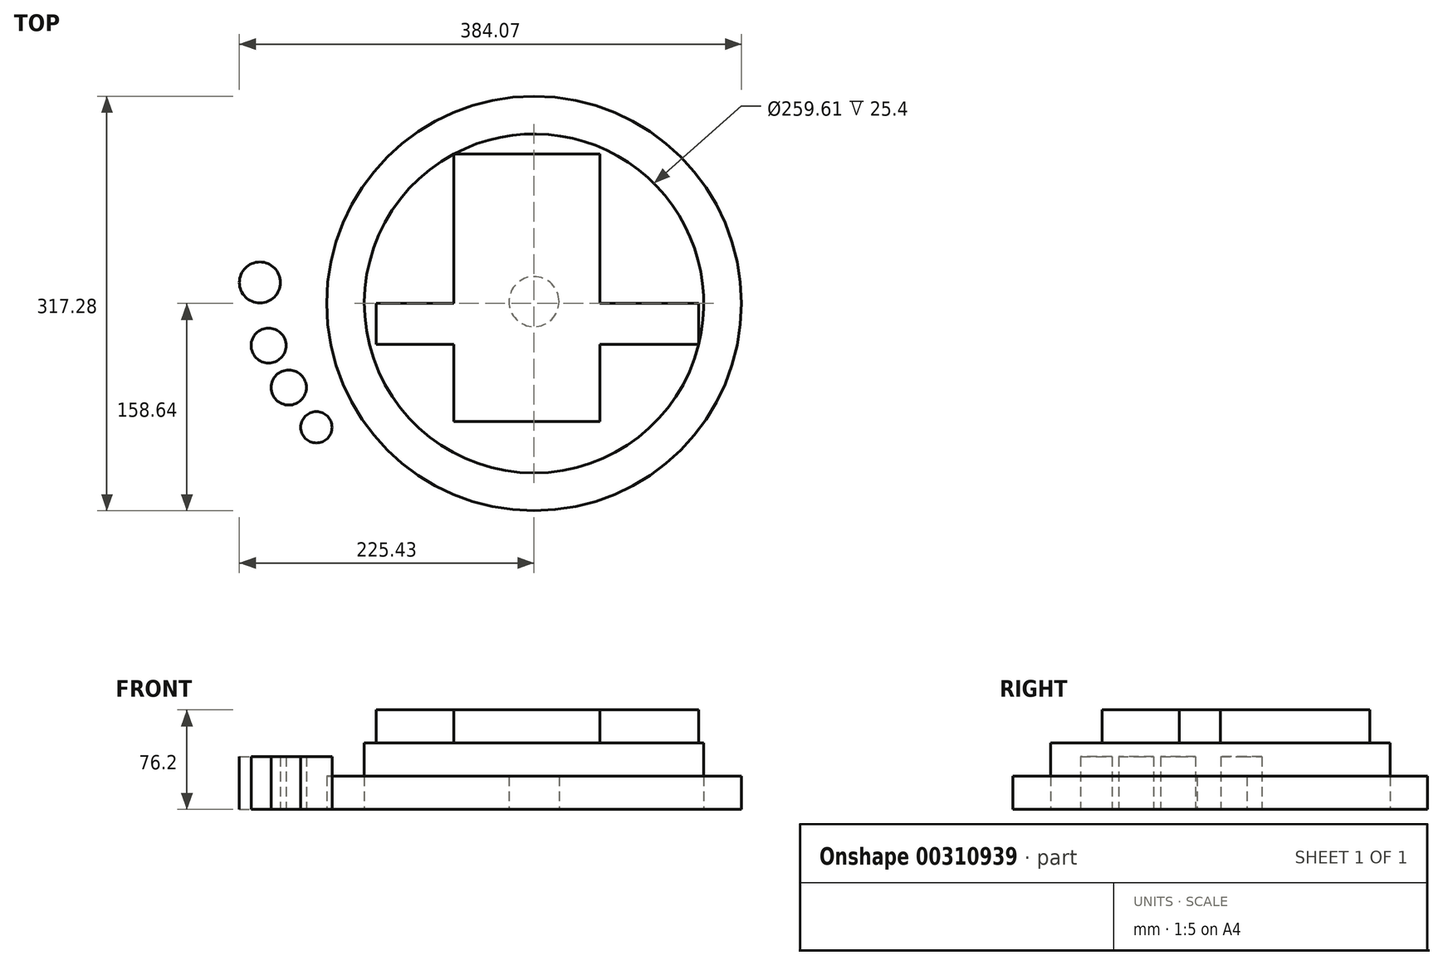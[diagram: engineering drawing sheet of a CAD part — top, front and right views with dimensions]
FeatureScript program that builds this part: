
annotation { "Feature Type Name" : "Feature", "Feature Type Description" : "" }
export const myFeature = defineFeature(function(context is Context, id is Id, definition is map)
    precondition{}
    {
        {
            var Q0;
            Q0=qCreatedBy(makeId("Top.planeOp"),FACE);
            var sketch = newSketch(context, id + "F0", { "sketchPlane" : qUnion([Q0])});
            skCircle(sketch, "E0", {"center": v(0, 0) * mm, "radius": 158.64 * mm});
            skCircle(sketch, "E1", {"center": v(0, 0) * mm, "radius": 129.8 * mm});
            skCircle(sketch, "E2", {"center": v(0, 1.4) * mm, "radius": 19.13 * mm});
            skSolve(sketch);
        }
        {
            var Q0;
            Q0=makeQuery(id+"F0.imprint","IMPRINT",FACE,{"disambiguationData":[TD([[makeQuery(id+"F0.imprint","IMPRINT",EDGE,{"derivedFrom":sQuery(id+"F0.wireOp",EDGE,"E0")}),1.0]])]});
            var Q1;
            Q1=makeQuery(id+"F0.imprint","IMPRINT",FACE,{"disambiguationData":[TD([[makeQuery(id+"F0.imprint","IMPRINT",EDGE,{"derivedFrom":sQuery(id+"F0.wireOp",EDGE,"E2")}),1.0]])]});
            extrude(context, id + "F1", {"entities" : qUnion([Q0, Q1]), "depth" : 25.4 * mm});
        }
        {
            var Q0;
            Q0=makeQuery(id+"F1.opExtrude","CAP_FACE",FACE,{"disambiguationData":[OSD([sQuery(id+"F0.wireOp",EDGE,"E0"),sQuery(id+"F0.wireOp",EDGE,"E1")])],"isStart":false});
            var sketch = newSketch(context, id + "F2", { "sketchPlane" : qUnion([Q0])});
            skLineSegment(sketch, "E3.bottom", {"start": v(-51.15, -187.93) * mm, "end": v(0, -187.93) * mm, "construction": true});
            skLineSegment(sketch, "E3.top", {"start": v(-51.15, -158.64) * mm, "end": v(0, -158.64) * mm});
            skLineSegment(sketch, "E3.left", {"start": v(-51.15, -187.93) * mm, "end": v(-51.15, -158.64) * mm});
            skLineSegment(sketch, "E3.right", {"start": v(0, -187.93) * mm, "end": v(0, -158.64) * mm});
            skSolve(sketch);
        }
        {
            var Q0;
            Q0=makeQuery(id+"F1.opExtrude","CAP_FACE",FACE,{"disambiguationData":[OSD([sQuery(id+"F0.wireOp",EDGE,"E0"),sQuery(id+"F0.wireOp",EDGE,"E1")])],"isStart":true});
            var sketch = newSketch(context, id + "F3", { "sketchPlane" : qUnion([Q0])});
            skCircle(sketch, "E4", {"center": v(-209.7, -16.02) * mm, "radius": 15.73 * mm});
            skCircle(sketch, "E5", {"center": v(-203.06, 32.24) * mm, "radius": 13.36 * mm});
            skCircle(sketch, "E6", {"center": v(-187.62, 64.35) * mm, "radius": 13.45 * mm});
            skCircle(sketch, "E7", {"center": v(-166.5, 94.78) * mm, "radius": 12 * mm});
            skSolve(sketch);
        }
        {
            var Q0;
            Q0=qSketchRegion(id+"F3",true);
            extrude(context, id + "F4", {"entities" : qUnion([Q0]), "oppositeDirection" : true, "depth" : 40.4 * mm});
        }
        {
            var Q0;
            Q0=makeQuery(id+"F2.imprint","IMPRINT",FACE,{"disambiguationData":[TD([[makeQuery(id+"F2.imprint","IMPRINT",EDGE,{"derivedFrom":makeQuery(id+"F1.opExtrude","CAP_EDGE",EDGE,{"disambiguationData":[OSD([sQuery(id+"F0.wireOp",EDGE,"E1")])],"isStart":false})}),1.0]])]});
            var sketch = newSketch(context, id + "F5", { "sketchPlane" : qUnion([Q0])});
            skLineSegment(sketch, "E8.bottom", {"start": v(24.96, 0) * mm, "end": v(119.1, 0) * mm});
            skLineSegment(sketch, "E8.top", {"start": v(24.96, -13.72) * mm, "end": v(119.1, -13.72) * mm});
            skLineSegment(sketch, "E8.left", {"start": v(24.96, 0) * mm, "end": v(24.96, -13.72) * mm});
            skLineSegment(sketch, "E8.right", {"start": v(119.1, 0) * mm, "end": v(119.1, -13.72) * mm});
            skLineSegment(sketch, "E9.bottom", {"start": v(-15.34, -6.31) * mm, "end": v(-86.15, -6.31) * mm});
            skLineSegment(sketch, "E9.top", {"start": v(-15.34, 8.98) * mm, "end": v(-86.15, 8.98) * mm});
            skLineSegment(sketch, "E9.left", {"start": v(-15.34, -6.31) * mm, "end": v(-15.34, 8.98) * mm});
            skLineSegment(sketch, "E9.right", {"start": v(-86.15, -6.31) * mm, "end": v(-86.15, 8.98) * mm});
            skLineSegment(sketch, "E10.bottom", {"start": v(0, 18.73) * mm, "end": v(-19.37, 18.73) * mm});
            skLineSegment(sketch, "E10.top", {"start": v(0, 75.02) * mm, "end": v(-19.37, 75.02) * mm});
            skLineSegment(sketch, "E10.left", {"start": v(0, 18.73) * mm, "end": v(0, 75.02) * mm});
            skLineSegment(sketch, "E10.right", {"start": v(-19.37, 18.73) * mm, "end": v(-19.37, 75.02) * mm});
            skPoint(sketch, "E11.firstSnap0", {"position": v(0, 46.87) * mm});
            skPoint(sketch, "E11.oppositeSnap0", {"position": v(24.96, -6.86) * mm});
            skLineSegment(sketch, "E11.bottom", {"start": v(0, -13.72) * mm, "end": v(24.96, -13.72) * mm});
            skLineSegment(sketch, "E11.top", {"start": v(0, -79.26) * mm, "end": v(24.96, -79.26) * mm});
            skLineSegment(sketch, "E11.left", {"start": v(0, -13.72) * mm, "end": v(0, -79.26) * mm});
            skLineSegment(sketch, "E11.right", {"start": v(24.96, -13.72) * mm, "end": v(24.96, -79.26) * mm});
            skSolve(sketch);
        }
        {
            var Q0;
            Q0=makeQuery(id+"F5.imprint","IMPRINT",FACE,{"disambiguationData":[TD([[makeQuery(id+"F5.imprint","IMPRINT",EDGE,{"derivedFrom":sQuery(id+"F5.wireOp",EDGE,"E8.bottom")}),-1.0]])]});
            var Q1;
            Q1=makeQuery(id+"F5.imprint","IMPRINT",FACE,{"disambiguationData":[TD([[makeQuery(id+"F5.imprint","IMPRINT",EDGE,{"derivedFrom":sQuery(id+"F5.wireOp",EDGE,"E11.bottom")}),-1.0]])]});
            var Q2;
            Q2=makeQuery(id+"F5.imprint","IMPRINT",FACE,{"disambiguationData":[TD([[makeQuery(id+"F5.imprint","IMPRINT",EDGE,{"derivedFrom":sQuery(id+"F5.wireOp",EDGE,"E10.bottom")}),-1.0]])]});
            var Q3;
            Q3=makeQuery(id+"F2.imprint","IMPRINT",FACE,{"disambiguationData":[TD([[makeQuery(id+"F2.imprint","IMPRINT",EDGE,{"derivedFrom":makeQuery(id+"F1.opExtrude","CAP_EDGE",EDGE,{"disambiguationData":[OSD([sQuery(id+"F0.wireOp",EDGE,"E1")])],"isStart":false})}),1.0]])]});
            extrude(context, id + "F6", {"entities" : qUnion([Q0, Q1, Q2, Q3]), "operationType" : NewBodyOperationType.ADD, "depth" : 25.4 * mm});
        }
        {
            var Q0;
            Q0=makeQuery(id+"F6.opExtrude","CAP_FACE",FACE,{"disambiguationData":[OSD([sQuery(id+"F0.wireOp",EDGE,"E1")])],"isStart":false});
            var sketch = newSketch(context, id + "F7", { "sketchPlane" : qUnion([Q0])});
            skLineSegment(sketch, "E12.bottom", {"start": v(-120.86, 0) * mm, "end": v(125.94, 0) * mm});
            skLineSegment(sketch, "E12.top", {"start": v(-120.86, -31.46) * mm, "end": v(125.94, -31.46) * mm});
            skLineSegment(sketch, "E12.left", {"start": v(-120.86, 0) * mm, "end": v(-120.86, -31.46) * mm});
            skLineSegment(sketch, "E12.right", {"start": v(125.94, 0) * mm, "end": v(125.94, -31.46) * mm});
            skLineSegment(sketch, "E13.bottom", {"start": v(50.53, -90.26) * mm, "end": v(-61.22, -90.26) * mm});
            skLineSegment(sketch, "E13.top", {"start": v(50.53, 114.47) * mm, "end": v(-61.22, 114.47) * mm});
            skLineSegment(sketch, "E13.left", {"start": v(50.53, -90.26) * mm, "end": v(50.53, 114.47) * mm});
            skLineSegment(sketch, "E13.right", {"start": v(-61.22, -90.26) * mm, "end": v(-61.22, 114.47) * mm});
            skSolve(sketch);
        }
        {
            var Q0;
            Q0=qSketchRegion(id+"F7",true);
            extrude(context, id + "F8", {"entities" : qUnion([Q0]), "operationType" : NewBodyOperationType.ADD, "depth" : 25.4 * mm});
        }
    });
